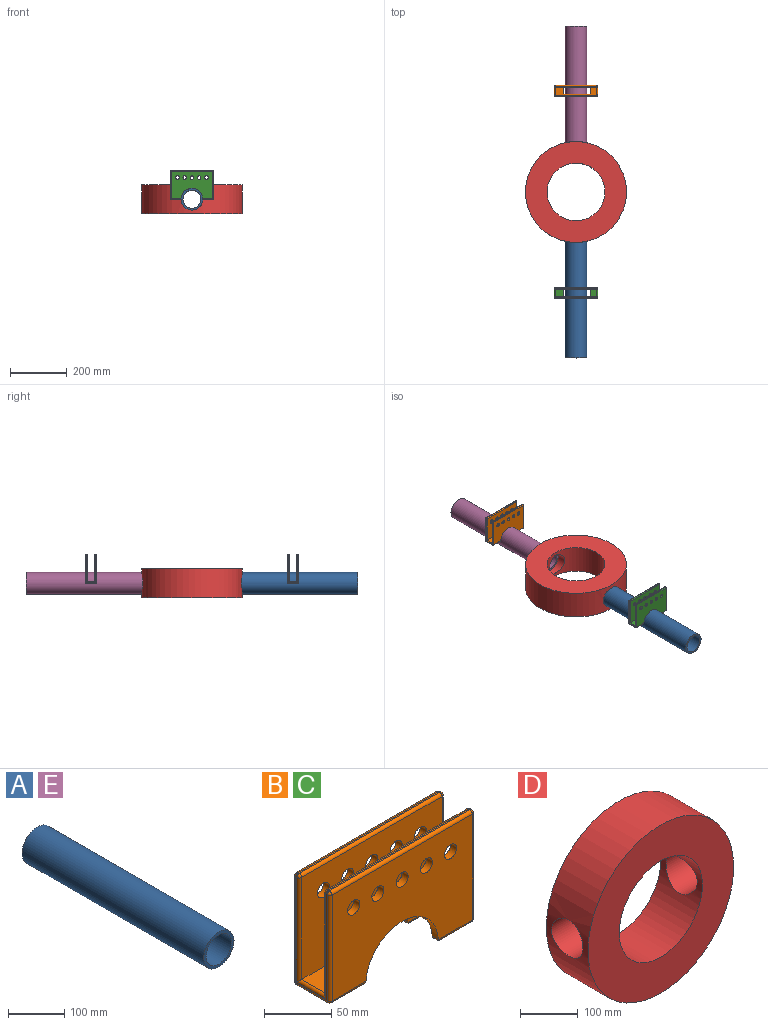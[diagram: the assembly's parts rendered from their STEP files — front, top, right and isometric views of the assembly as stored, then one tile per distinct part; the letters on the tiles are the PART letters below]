
ASSEMBLY  parts=5 mates=4
PART A: 4 faces, bbox 76.2x457.2x76.2 mm
  f0: cylinder r=31.75mm len=457.2mm, axis (0,1,0), area 91207.3mm2, adj f2,f3
  f1: cylinder r=38.1mm len=457.2mm, axis (0,1,0), area 109448.8mm2, adj f2,f3
  f2: plane 76.2x76.2mm, normal (0,-1,0), area 1393.4mm2, adj f0,f1
  f3: plane 76.2x76.2mm, normal (0,1,0), area 1393.4mm2, adj f0,f1
PART B: 72 faces, bbox 152.4x38.1x101.6 mm
  f0: plane 33.1x33.02mm, normal (0,0,-1), area 897mm2, adj f43,f45,f46,f49,f50,f54,f57,f58
  f1: plane 147.32x1.27mm, normal (0,0,1), area 187.1mm2, adj f31,f47,f55,f56
  f2: plane 96.52x33.02mm, normal (-1,0,0), area 283.9mm2, adj f48,f56,f57,f62,f63,f65,f67,f68
  f3: plane 96.52x33.02mm, normal (1,0,0), area 283.9mm2, adj f26,f27,f28,f29,f30,f31,f33,f34
  f4: plane 33.1x33.02mm, normal (0,0,-1), area 703.4mm2, adj f34,f35,f37,f38,f39,f40,f41,f42
  f5: cylinder r=6.35mm len=12.7mm, axis (0,1,0), area 253.4mm2, adj f10,f15
  f6: cylinder r=6.35mm len=12.7mm, axis (0,1,0), area 253.4mm2, adj f10,f15
  f7: cylinder r=6.35mm len=12.7mm, axis (0,1,0), area 253.4mm2, adj f10,f15
  f8: cylinder r=6.35mm len=12.7mm, axis (0,1,0), area 253.4mm2, adj f10,f15
  f9: cylinder r=6.35mm len=12.7mm, axis (0,1,0), area 253.4mm2, adj f10,f15
  f10: plane 147.32x96.52mm, normal (0,1,0), area 11300.8mm2, adj f5,f6,f7,f8,f9,f11,f12,f13
  f11: plane 25.4x22.86mm, normal (0,0,1), area 580.6mm2, adj f10,f12,f18,f27
  f12: plane 25.4x3.81mm, normal (-1,0,0), area 96.8mm2, adj f10,f11,f18,f41
  f13: plane 29.21x25.4mm, normal (0,0,1), area 741.9mm2, adj f10,f14,f18,f65
  f14: plane 25.4x3.81mm, normal (1,0,0), area 96.8mm2, adj f10,f13,f18,f46
  f15: plane 147.32x96.52mm, normal (0,-1,0), area 11499.2mm2, adj f5,f6,f7,f8,f9,f20,f33,f38
  f16: plane 147.32x1.27mm, normal (0,0,1), area 187.1mm2, adj f28,f64,f68,f70
  f17: plane 147.32x96.52mm, normal (0,1,0), area 11499.2mm2, adj f19,f21,f22,f23,f24,f25,f30,f35
  f18: plane 147.32x96.52mm, normal (0,-1,0), area 11300.8mm2, adj f11,f12,f13,f14,f19,f21,f22,f23
  f19: cylinder r=38.1mm len=76.05mm, axis (0,-1,0), area 729.8mm2, adj f17,f18,f35,f37,f39,f50,f54,f58
  f20: cylinder r=38.1mm len=76.05mm, axis (0,-1,0), area 729.8mm2, adj f10,f15,f38,f40,f42,f43,f45,f49
  f21: cylinder r=6.35mm len=12.7mm, axis (0,-1,0), area 253.4mm2, adj f17,f18
  f22: cylinder r=6.35mm len=12.7mm, axis (0,-1,0), area 253.4mm2, adj f17,f18
  f23: cylinder r=6.35mm len=12.7mm, axis (0,-1,0), area 253.4mm2, adj f17,f18
  f24: cylinder r=6.35mm len=12.7mm, axis (0,-1,0), area 253.4mm2, adj f17,f18
  f25: cylinder r=6.35mm len=12.7mm, axis (0,-1,0), area 253.4mm2, adj f17,f18
  f26: cylinder r=2.54mm len=95.25mm, axis (0,0,1), area 373.6mm2, adj f3,f18,f27,f71
  f27: cylinder r=2.54mm len=30.48mm, axis (0,-1,0), area 108.7mm2, adj f3,f11,f26,f29
  f28: cylinder r=2.54mm len=2.54mm, axis (0,1,0), area 5.1mm2, adj f3,f16,f61,f71
  f29: cylinder r=2.54mm len=95.25mm, axis (0,0,1), area 373.6mm2, adj f3,f10,f27,f51
  f30: cylinder r=2.54mm len=96.52mm, axis (0,0,-1), area 385.1mm2, adj f3,f17,f32,f61
  f31: cylinder r=2.54mm len=2.54mm, axis (0,1,0), area 5.1mm2, adj f1,f3,f44,f51
  f32: sphere r=2.54mm, area 10.1mm2, adj f30,f34,f35
  f33: cylinder r=2.54mm len=96.52mm, axis (0,0,-1), area 385.1mm2, adj f3,f15,f36,f44
  f34: cylinder r=2.54mm len=33.02mm, axis (0,-1,0), area 131.7mm2, adj f3,f4,f32,f36
  f35: cylinder r=2.54mm len=35.64mm, axis (1,0,0), area 138.5mm2, adj f4,f17,f19,f32,f37
  f36: sphere r=2.54mm, area 10.1mm2, adj f33,f34,f38
  f37: cylinder r=2.54mm len=6.34mm, axis (0,-1,0), area 17mm2, adj f4,f19,f35,f39
  f38: cylinder r=2.54mm len=35.64mm, axis (-1,0,0), area 138.5mm2, adj f4,f15,f20,f36,f40
  f39: cylinder r=2.54mm len=15.32mm, axis (-1,0,0), area 51mm2, adj f4,f18,f19,f37,f41
  f40: cylinder r=2.54mm len=6.34mm, axis (0,-1,0), area 17mm2, adj f4,f20,f38,f42
  f41: cylinder r=2.54mm len=30.48mm, axis (0,-1,0), area 108.7mm2, adj f4,f12,f39,f42
  f42: cylinder r=2.54mm len=15.32mm, axis (1,0,0), area 51mm2, adj f4,f10,f20,f40,f41
  f43: cylinder r=2.54mm len=8.97mm, axis (1,0,0), area 25.7mm2, adj f0,f10,f20,f45,f46
  f44: sphere r=2.54mm, area 10.1mm2, adj f31,f33,f47
  f45: cylinder r=2.54mm len=6.34mm, axis (0,-1,0), area 17mm2, adj f0,f20,f43,f49
  f46: cylinder r=2.54mm len=30.48mm, axis (0,1,0), area 108.7mm2, adj f0,f14,f43,f50
  f47: cylinder r=2.54mm len=147.32mm, axis (1,0,0), area 587.8mm2, adj f1,f15,f44,f52
  f48: cylinder r=2.54mm len=96.52mm, axis (0,0,1), area 385.1mm2, adj f2,f15,f52,f53
  f49: cylinder r=2.54mm len=35.64mm, axis (-1,0,0), area 138.5mm2, adj f0,f15,f20,f45,f53
  f50: cylinder r=2.54mm len=8.97mm, axis (-1,0,0), area 25.7mm2, adj f0,f18,f19,f46,f54
  f51: sphere r=2.54mm, area 10.1mm2, adj f29,f31,f55
  f52: sphere r=2.54mm, area 10.1mm2, adj f47,f48,f56
  f53: sphere r=2.54mm, area 10.1mm2, adj f48,f49,f57
  f54: cylinder r=2.54mm len=6.34mm, axis (0,-1,0), area 17mm2, adj f0,f19,f50,f58
  f55: cylinder r=2.54mm len=147.32mm, axis (-1,0,0), area 587.8mm2, adj f1,f10,f51,f59
  f56: cylinder r=2.54mm len=2.54mm, axis (0,-1,0), area 5.1mm2, adj f1,f2,f52,f59
  f57: cylinder r=2.54mm len=33.02mm, axis (0,1,0), area 131.7mm2, adj f0,f2,f53,f60
  f58: cylinder r=2.54mm len=35.64mm, axis (1,0,0), area 138.5mm2, adj f0,f17,f19,f54,f60
  f59: sphere r=2.54mm, area 10.1mm2, adj f55,f56,f62
  f60: sphere r=2.54mm, area 10.1mm2, adj f57,f58,f63
  f61: sphere r=2.54mm, area 10.1mm2, adj f28,f30,f64
  f62: cylinder r=2.54mm len=95.25mm, axis (0,0,-1), area 373.6mm2, adj f2,f10,f59,f65
  f63: cylinder r=2.54mm len=96.52mm, axis (0,0,1), area 385.1mm2, adj f2,f17,f60,f66
  f64: cylinder r=2.54mm len=147.32mm, axis (1,0,0), area 587.8mm2, adj f16,f17,f61,f66
  f65: cylinder r=2.54mm len=30.48mm, axis (0,-1,0), area 108.7mm2, adj f2,f13,f62,f67
  f66: sphere r=2.54mm, area 10.1mm2, adj f63,f64,f68
  f67: cylinder r=2.54mm len=95.25mm, axis (0,0,-1), area 373.6mm2, adj f2,f18,f65,f69
  f68: cylinder r=2.54mm len=2.54mm, axis (0,-1,0), area 5.1mm2, adj f2,f16,f66,f69
  f69: sphere r=2.54mm, area 10.1mm2, adj f67,f68,f70
  f70: cylinder r=2.54mm len=147.32mm, axis (-1,0,0), area 587.8mm2, adj f16,f18,f69,f71
  f71: sphere r=2.54mm, area 10.1mm2, adj f26,f28,f70
PART C: same geometry as B
PART D: 6 faces, bbox 355.6x101.6x355.6 mm
  f0: cylinder r=177.8mm len=355.6mm, axis (0,1,0), area 104332.6mm2, adj f1,f2,f4,f5
  f1: plane 355.6x355.6mm, normal (0,-1,0), area 66885.4mm2, adj f0,f3
  f2: plane 355.6x355.6mm, normal (0,1,0), area 66885.4mm2, adj f0,f3
  f3: cylinder r=101.6mm len=203.2mm, axis (0,1,0), area 55548.1mm2, adj f1,f2,f4,f5
  f4: cylinder r=38.1mm len=83.62mm, axis (1,0,0), area 18628.6mm2, adj f0,f3
  f5: cylinder r=38.1mm len=83.62mm, axis (1,0,0), area 18625.9mm2, adj f0,f3
PART E: same geometry as A
PLACE A rot(axis=(0,1,0),90deg) t=(-52.09,134.9,110.66)mm
PLACE B rot(axis=(1,0,0),0deg) t=(-63.02,605.91,643.7)mm
PLACE C rot(axis=(1,0,0),0deg) t=(-63.02,-106.4,643.7)mm
PLACE D rot(axis=(-0.58,-0.58,0.58),120deg) t=(-52.09,262.45,110.66)mm
PLACE E rot(axis=(0,0,1),180deg) t=(-52.09,390.01,110.66)mm
MATE fastened D.f4 <-> E.f0  axis (0,1,0) through (-52.09,440.81,110.66)mm
MATE fastened C.f19 <-> A.f1  axis (0,1,0) through (-52.09,-74.65,110.66)mm
MATE fastened A.f0 <-> D.f4  axis (0,1,0) through (-52.09,134.9,110.66)mm
MATE fastened B.f19 <-> E.f1  axis (0,1,0) through (-52.09,637.66,110.66)mm
